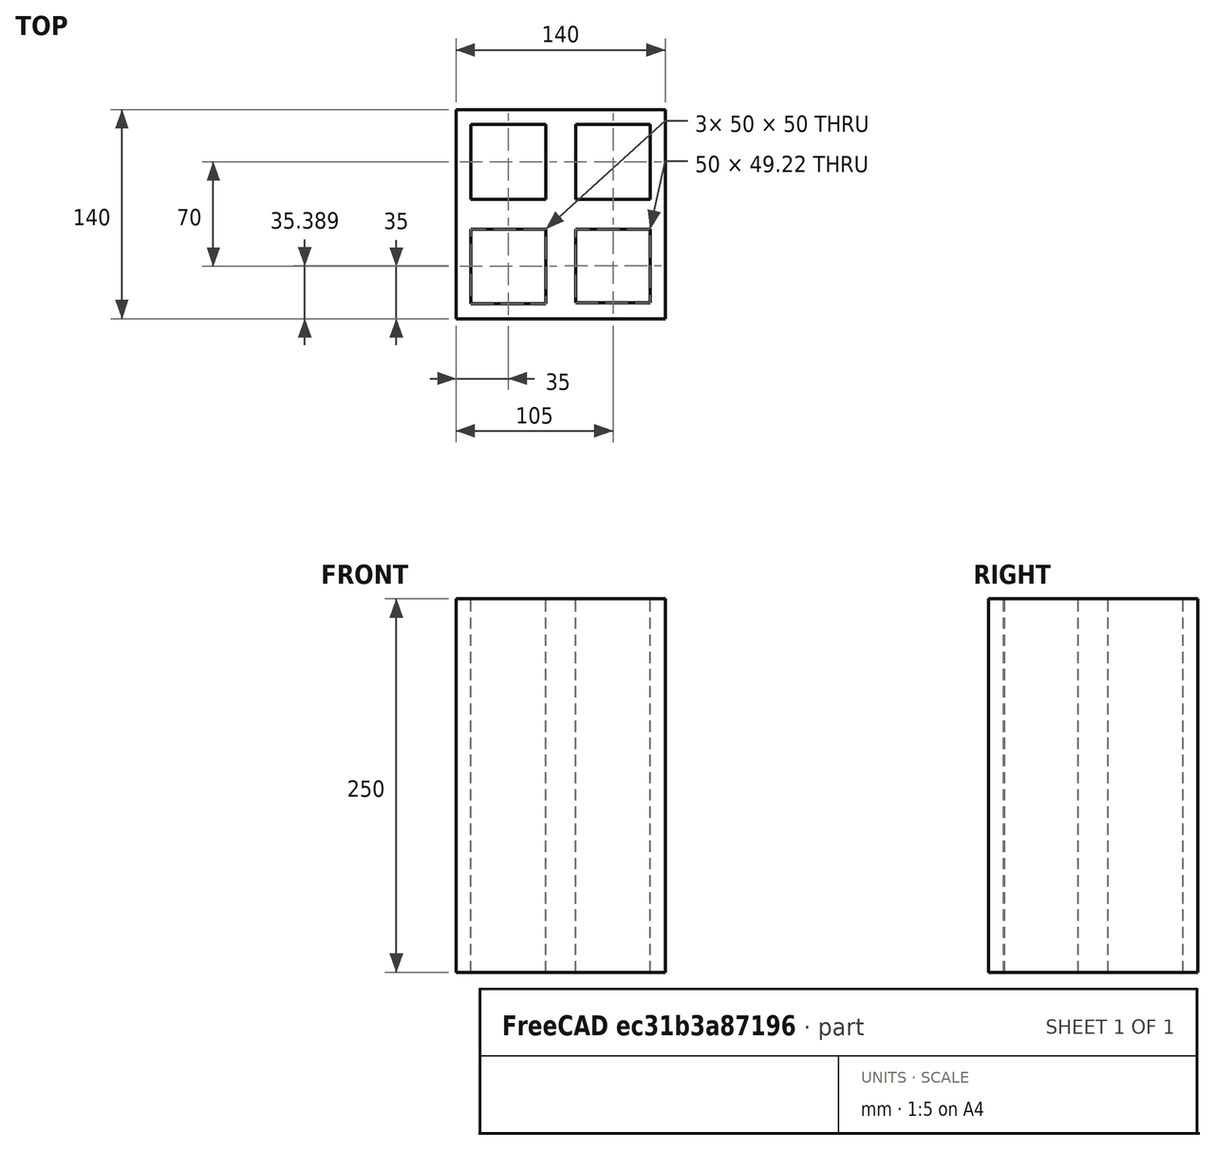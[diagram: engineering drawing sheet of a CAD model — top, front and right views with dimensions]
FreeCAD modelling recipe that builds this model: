
FCSTD DOCUMENT  (FreeCAD 0.21R33694 (Git))
Label: OJT1_T018_Ladrillo
License: All rights reserved
LicenseURL: https://en.wikipedia.org/wiki/All_rights_reserved
objects: Sketcher::SketchObject×1, PartDesign::Pad×1, PartDesign::Body×1
note: 4 computed .brp shape members not serialized (recipe doc carries the construction recipe); baked Part::Feature solids carry a one-line shape summary decoded from their .brp

FEATURE [Sketcher::SketchObject] Sketch
  FullyConstrained = false
  MapMode = 5
  Support = -> [XY_Plane]
  sketch-geometry (20):
    g0: LineSegment StartX=-70 StartY=70 StartZ=0 EndX=70 EndY=70 EndZ=0
    g1: LineSegment StartX=70 StartY=70 StartZ=0 EndX=70 EndY=-70 EndZ=0
    g2: LineSegment StartX=70 StartY=-70 StartZ=0 EndX=-70 EndY=-70 EndZ=0
    g3: LineSegment StartX=-70 StartY=-70 StartZ=0 EndX=-70 EndY=70 EndZ=0
    g4: LineSegment StartX=-60 StartY=60 StartZ=0 EndX=-10 EndY=60 EndZ=0
    g5: LineSegment StartX=-10 StartY=60 StartZ=0 EndX=-10 EndY=10 EndZ=0
    g6: LineSegment StartX=-10 StartY=10 StartZ=0 EndX=-60 EndY=10 EndZ=0
    g7: LineSegment StartX=-60 StartY=10 StartZ=0 EndX=-60 EndY=60 EndZ=0
    g8: LineSegment StartX=10 StartY=60 StartZ=0 EndX=60 EndY=60 EndZ=0
    g9: LineSegment StartX=60 StartY=60 StartZ=0 EndX=60 EndY=10 EndZ=0
    g10: LineSegment StartX=60 StartY=10 StartZ=0 EndX=10 EndY=10 EndZ=0
    g11: LineSegment StartX=10 StartY=10 StartZ=0 EndX=10 EndY=60 EndZ=0
    g12: LineSegment StartX=-60 StartY=-10 StartZ=0 EndX=-10 EndY=-10 EndZ=0
    g13: LineSegment StartX=-10 StartY=-10 StartZ=0 EndX=-10 EndY=-60 EndZ=0
    g14: LineSegment StartX=-10 StartY=-60 StartZ=0 EndX=-60 EndY=-60 EndZ=0
    g15: LineSegment StartX=-60 StartY=-60 StartZ=0 EndX=-60 EndY=-10 EndZ=0
    g16: LineSegment StartX=10 StartY=-10 StartZ=0 EndX=60 EndY=-10 EndZ=0
    g17: LineSegment StartX=60 StartY=-10 StartZ=0 EndX=60 EndY=-59.2227 EndZ=0
    g18: LineSegment StartX=60 StartY=-59.2227 StartZ=0 EndX=10 EndY=-59.2227 EndZ=0
    g19: LineSegment StartX=10 StartY=-59.2227 StartZ=0 EndX=10 EndY=-10 EndZ=0
  constraints (54):
    c: Coincident(g0,g1)
    c: Coincident(g1,g2)
    c: Coincident(g2,g3)
    c: Coincident(g3,g0)
    c: Horizontal(g2)
    c: Vertical(g1)
    c: Vertical(g3)
    c: Coincident(g4,g5)
    c: Coincident(g5,g6)
    c: Coincident(g6,g7)
    c: Coincident(g7,g4)
    c: Horizontal(g4)
    c: Horizontal(g6)
    c: Vertical(g5)
    c: Vertical(g7)
    c: Coincident(g8,g9)
    c: Coincident(g9,g10)
    c: Coincident(g10,g11)
    c: Coincident(g11,g8)
    c: Horizontal(g8)
    c: Horizontal(g10)
    c: Vertical(g9)
    c: Vertical(g11)
    c: Coincident(g12,g13)
    c: Coincident(g13,g14)
    c: Coincident(g14,g15)
    c: Coincident(g15,g12)
    c: Horizontal(g12)
    c: Horizontal(g14)
    c: Vertical(g13)
    c: Coincident(g16,g17)
    c: Coincident(g17,g18)
    c: Coincident(g18,g19)
    c: Coincident(g19,g16)
    c: Horizontal(g16)
    c: Horizontal(g18)
    c: Vertical(g17)
    c: Vertical(g19)
    c: Symmetric(g4,g8,g-2)
    c: Symmetric(g6,g12,g-1)
    c: Symmetric(g12,g16,g-2)
    c: Symmetric(g0,g0,g-2)
    c: Symmetric(g4,g14,g-1)
    c: DistanceX(g0,g0) = 140
    c: DistanceY(g3,g3) = 140
    c: DistanceX(g0,g4) = 10
    c: DistanceY(g4,g0) = 10
    c: DistanceY(g2,g14) = 10
    c: DistanceX(g12,g12) = 50
    c: Equal(g12,g6)
    c: DistanceY(g13,g13) = 50
    c: Equal(g13,g11)
    c: Equal(g12,g10)
    c: Equal(g12,g18)
FEATURE [PartDesign::Pad] Pad
  Direction = (0,0,1)
  Length = 250
  Length2 = 10
  Profile = -> Sketch
  ReferenceAxis = -> Sketch [N_Axis]
  Type = 0
FEATURE [PartDesign::Body] Body
  Group = -> [Sketch,Pad]
  Origin = -> Origin
  Tip = -> Pad
